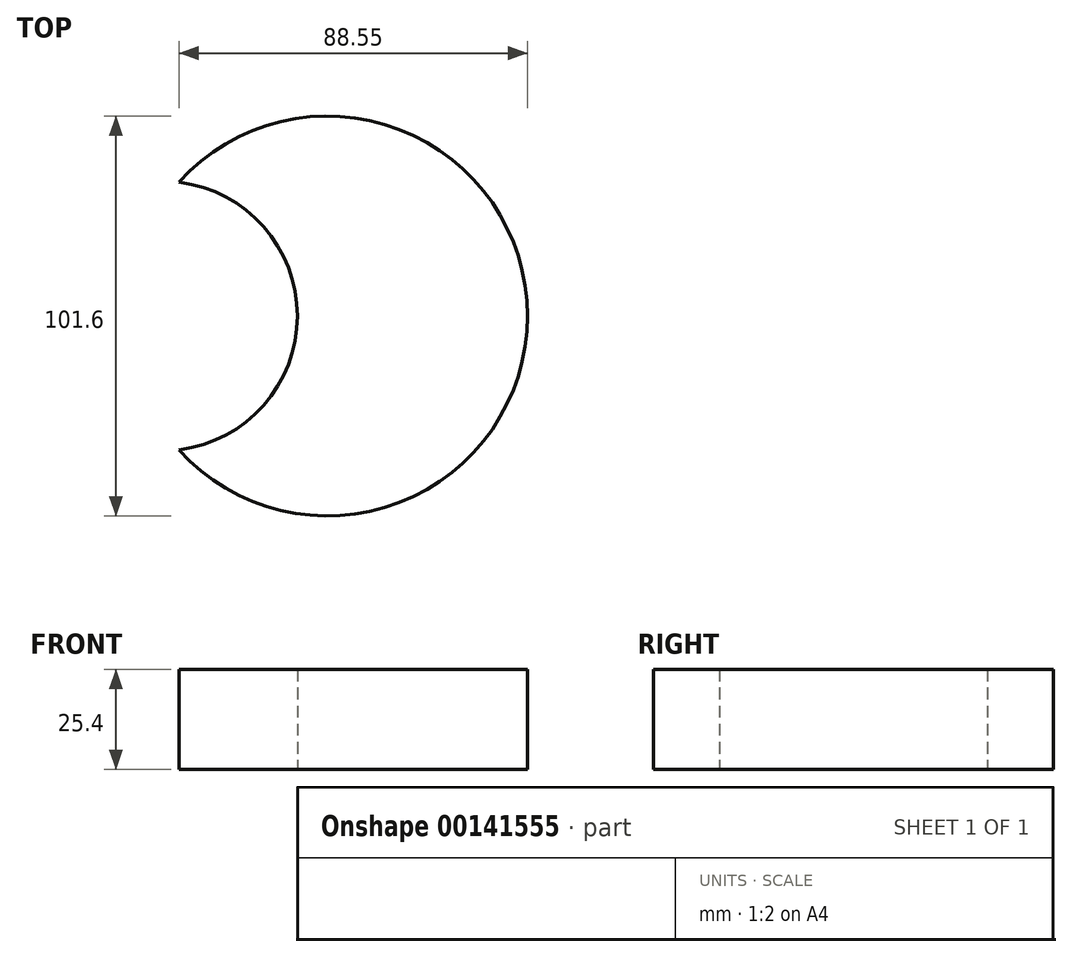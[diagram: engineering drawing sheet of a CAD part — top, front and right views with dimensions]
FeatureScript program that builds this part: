
annotation { "Feature Type Name" : "Feature", "Feature Type Description" : "" }
export const myFeature = defineFeature(function(context is Context, id is Id, definition is map)
    precondition{}
    {
        {
            var Q0;
            Q0=qCreatedBy(makeId("Top.planeOp"),FACE);
            var sketch = newSketch(context, id + "F0", { "sketchPlane" : qUnion([Q0])});
            skArc(sketch, "E0", {"start": v(-37.75, -34) * mm, "mid": v(50.8, 0) * mm, "end": v(-37.75, 34) * mm});
            skArc(sketch, "E1", {"start": v(-37.75, -34) * mm, "mid": v(-7.66, 0) * mm, "end": v(-37.75, 34) * mm});
            skSolve(sketch);
        }
        {
            var Q0;
            Q0 = qSketchRegion(id + "F0", true);
            extrude(context, id + "F1", {"entities" : qUnion([Q0]), "depth" : 25.4 * mm});
        }
    });
